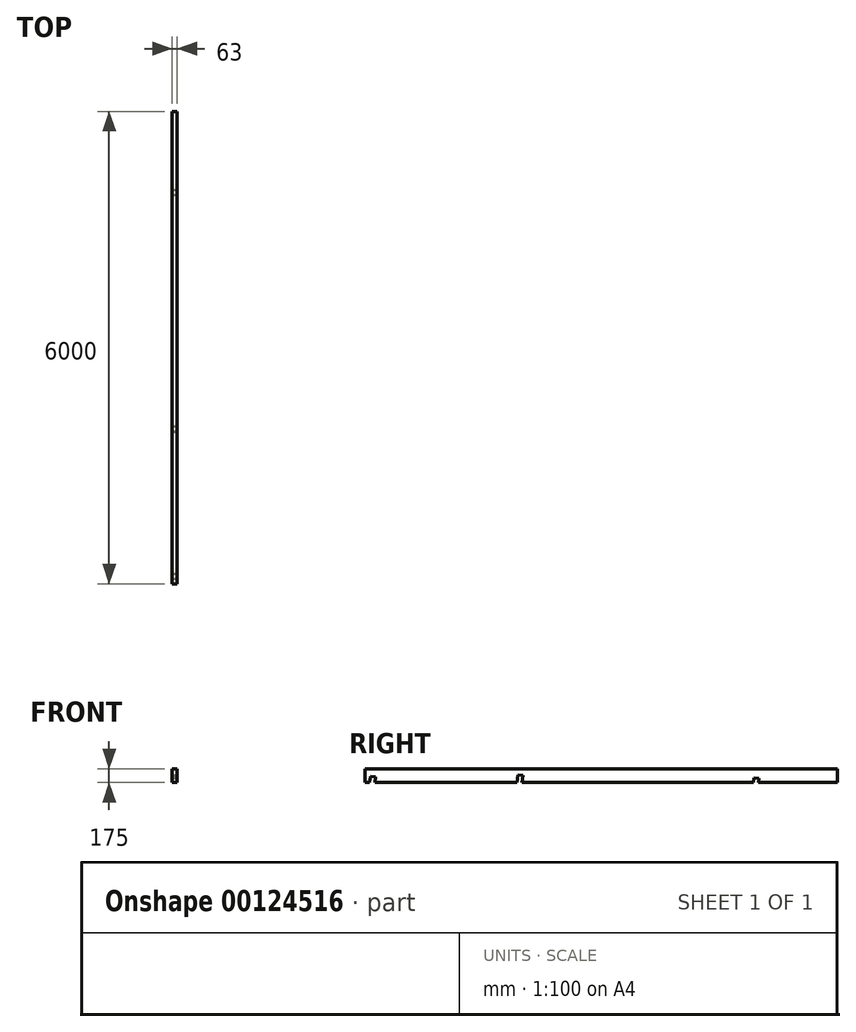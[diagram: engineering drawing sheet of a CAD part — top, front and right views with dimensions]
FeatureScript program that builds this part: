
annotation { "Feature Type Name" : "Feature", "Feature Type Description" : "" }
export const myFeature = defineFeature(function(context is Context, id is Id, definition is map)
    precondition{}
    {
        {
            var Q0;
            Q0=qCreatedBy(makeId("Front.planeOp"),FACE);
            var sketch = newSketch(context, id + "F0", { "sketchPlane" : qUnion([Q0])});
            skLineSegment(sketch, "E0.bottom", {"start": v(31.5, 87.5) * mm, "end": v(-31.5, 87.5) * mm});
            skLineSegment(sketch, "E0.top", {"start": v(31.5, -87.5) * mm, "end": v(-31.5, -87.5) * mm});
            skLineSegment(sketch, "E0.left", {"start": v(31.5, 87.5) * mm, "end": v(31.5, -87.5) * mm});
            skLineSegment(sketch, "E0.right", {"start": v(-31.5, 87.5) * mm, "end": v(-31.5, -87.5) * mm});
            skPoint(sketch, "E0.middle", {"position": v(0, 0) * mm});
            skSolve(sketch);
        }
        {
            var Q0;
            Q0=qSketchRegion(id+"F0",true);
            extrude(context, id + "F1", {"entities" : qUnion([Q0]), "endBound" : BoundingType.SYMMETRIC, "depth" : 6000 * mm});
        }
        {
            var Q0;
            Q0=makeQuery(id+"F1.opExtrude","SWEPT_FACE",FACE,{"disambiguationData":[OSD([sQuery(id+"F0.wireOp",EDGE,"E0.left")])]});
            var sketch = newSketch(context, id + "F2", { "sketchPlane" : qUnion([Q0])});
            skLineSegment(sketch, "E1", {"start": v(2000, -87.5) * mm, "end": v(2005.7, -37.5) * mm});
            skLineSegment(sketch, "E2", {"start": v(2005.7, -37.5) * mm, "end": v(1941.12, -30.14) * mm});
            skLineSegment(sketch, "E3", {"start": v(1941.12, -30.14) * mm, "end": v(1934.58, -87.5) * mm});
            skLineSegment(sketch, "E4", {"start": v(1934.58, -87.5) * mm, "end": v(2000, -87.5) * mm});
            skLineSegment(sketch, "E5", {"start": v(-1004.33, -87.5) * mm, "end": v(-994.07, 2.5) * mm});
            skLineSegment(sketch, "E6", {"start": v(-994.07, 2.5) * mm, "end": v(-1058.65, 9.86) * mm});
            skLineSegment(sketch, "E7", {"start": v(-1058.65, 9.86) * mm, "end": v(-1069.75, -87.5) * mm});
            skLineSegment(sketch, "E8", {"start": v(-1069.75, -87.5) * mm, "end": v(-1004.33, -87.5) * mm});
            skLineSegment(sketch, "E9", {"start": v(-2874.58, -87.5) * mm, "end": v(-2866.6, -17.5) * mm});
            skLineSegment(sketch, "E10", {"start": v(-2866.6, -17.5) * mm, "end": v(-2931.18, -10.14) * mm});
            skLineSegment(sketch, "E11", {"start": v(-2931.18, -10.14) * mm, "end": v(-2940, -87.5) * mm});
            skLineSegment(sketch, "E12", {"start": v(-2940, -87.5) * mm, "end": v(-2874.58, -87.5) * mm});
            skSolve(sketch);
        }
        {
            var Q0;
            Q0=qSketchRegion(id+"F2",true);
            extrude(context, id + "F3", {"entities" : qUnion([Q0]), "operationType" : NewBodyOperationType.REMOVE, "endBound" : BoundingType.UP_TO_NEXT, "oppositeDirection" : true, "depth" : 25 * mm});
        }
    });
